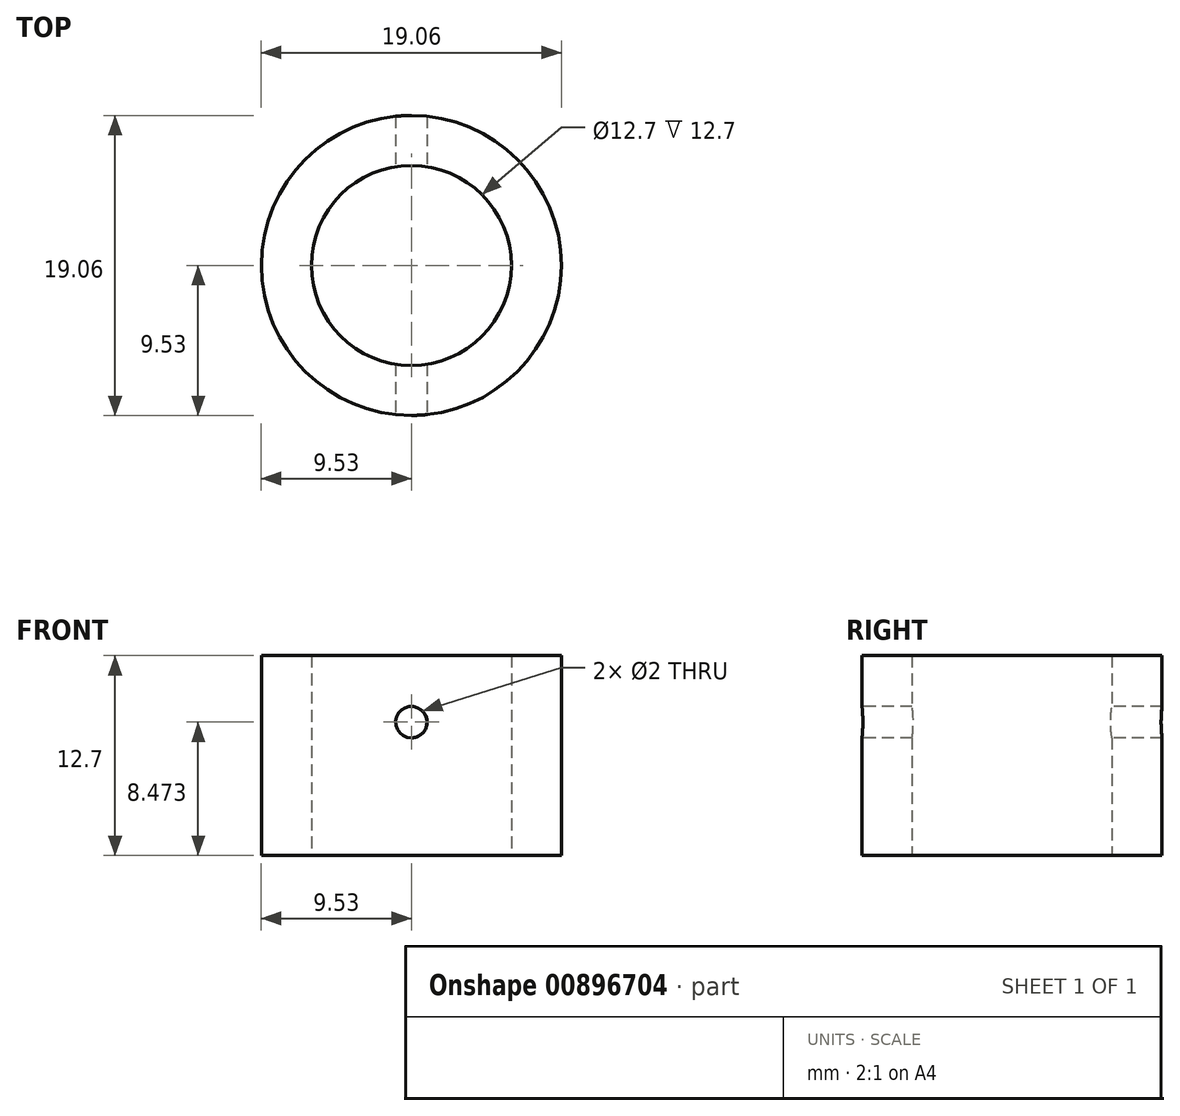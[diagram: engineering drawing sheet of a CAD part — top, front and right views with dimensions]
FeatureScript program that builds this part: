
annotation { "Feature Type Name" : "Feature", "Feature Type Description" : "" }
export const myFeature = defineFeature(function(context is Context, id is Id, definition is map)
    precondition{}
    {
        {
            var Q0;
            Q0=qCreatedBy(makeId("Top.planeOp"),FACE);
            var sketch = newSketch(context, id + "F0", { "sketchPlane" : qUnion([Q0])});
            skCircle(sketch, "E0", {"center": v(0, 0) * mm, "radius": 9.53 * mm});
            skCircle(sketch, "E1", {"center": v(0, 0) * mm, "radius": 6.35 * mm});
            skSolve(sketch);
        }
        {
            var Q0;
            Q0=makeQuery(id+"F0.imprint","IMPRINT",FACE,{"disambiguationData":[TD([[makeQuery(id+"F0.imprint","IMPRINT",EDGE,{"derivedFrom":sQuery(id+"F0.wireOp",EDGE,"E0")}),1.0]])]});
            extrude(context, id + "F1", {"entities" : qUnion([Q0]), "depth" : 12.7 * mm, "offsetDistance" : 25.4 * mm});
        }
        {
            var Q0;
            Q0=qCreatedBy(makeId("Front.planeOp"),FACE);
            var sketch = newSketch(context, id + "F2", { "sketchPlane" : qUnion([Q0])});
            skCircle(sketch, "E2", {"center": v(0, 8.47) * mm, "radius": 1 * mm});
            skSolve(sketch);
        }
        {
            var Q0;
            Q0 = qSketchRegion(id + "F2", true);
            extrude(context, id + "F3", {"entities" : qUnion([Q0]), "operationType" : NewBodyOperationType.REMOVE, "oppositeDirection" : true, "depth" : 25.4 * mm, "offsetDistance" : 25.4 * mm, "hasSecondDirection" : true, "secondDirectionOppositeDirection" : false, "secondDirectionDepth" : 25.4 * mm});
        }
    });
